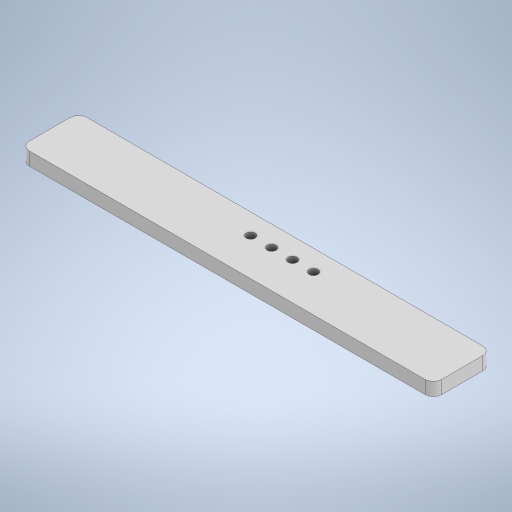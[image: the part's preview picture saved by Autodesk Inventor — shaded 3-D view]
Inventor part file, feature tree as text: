
AUTODESK INVENTOR PART (.ipt)
format: ipt  version: 2023.5 (Build 275446000, 446)  size: 302,592 bytes
history: native  units: mm
features: other x6, extrude x4, reference x4, fillet x2, sketch x2, projected_geometry x2
ambient origin geometry x8: Origin, YZ Plane, XZ Plane, XY Plane, X Axis, Y Axis, Z Axis, Center Point
bodies: Body1 (feature_tree)
feature tree (20):
  other  "Bryła1"
  extrude  "Wyciągnięcie proste1"  Depth=50.0mm
  fillet  "Zaokrąglenie1"  Radius=7.0mm
  extrude  "Wyciągnięcie proste2"  Depth=1.6mm TaperAngle=0.0deg
  extrude  "Wyciągnięcie proste3"  Depth=1.0mm
  fillet  "Zaokrąglenie3"  Radius=14.0mm
  extrude  "Wyciągnięcie proste4"  Depth=1.6mm TaperAngle=0.0deg
  sketch  "Szkic2"
  reference  "Odniesienie1"
  reference  "Odniesienie2"
  reference  "Odniesienie3"
  reference  "Odniesienie4"
  projected_geometry  "Pętla rzutowana2"
  sketch  "Szkic8"
  projected_geometry  "Pętla rzutowana3"
  parser-record x1  (decoder bookkeeping rows leaked as tree rows — omitted from the tree; the rows remain in map.json)
  other  "byk_v3.iam"
  other  "servo_mini_1370hd_cos:2"
  other  "servo_mini_1370hd_cos:1"
  other  "podstawa:1"
note: 1 file-system path scrubbed to <path> (originals preserved in map.json)
